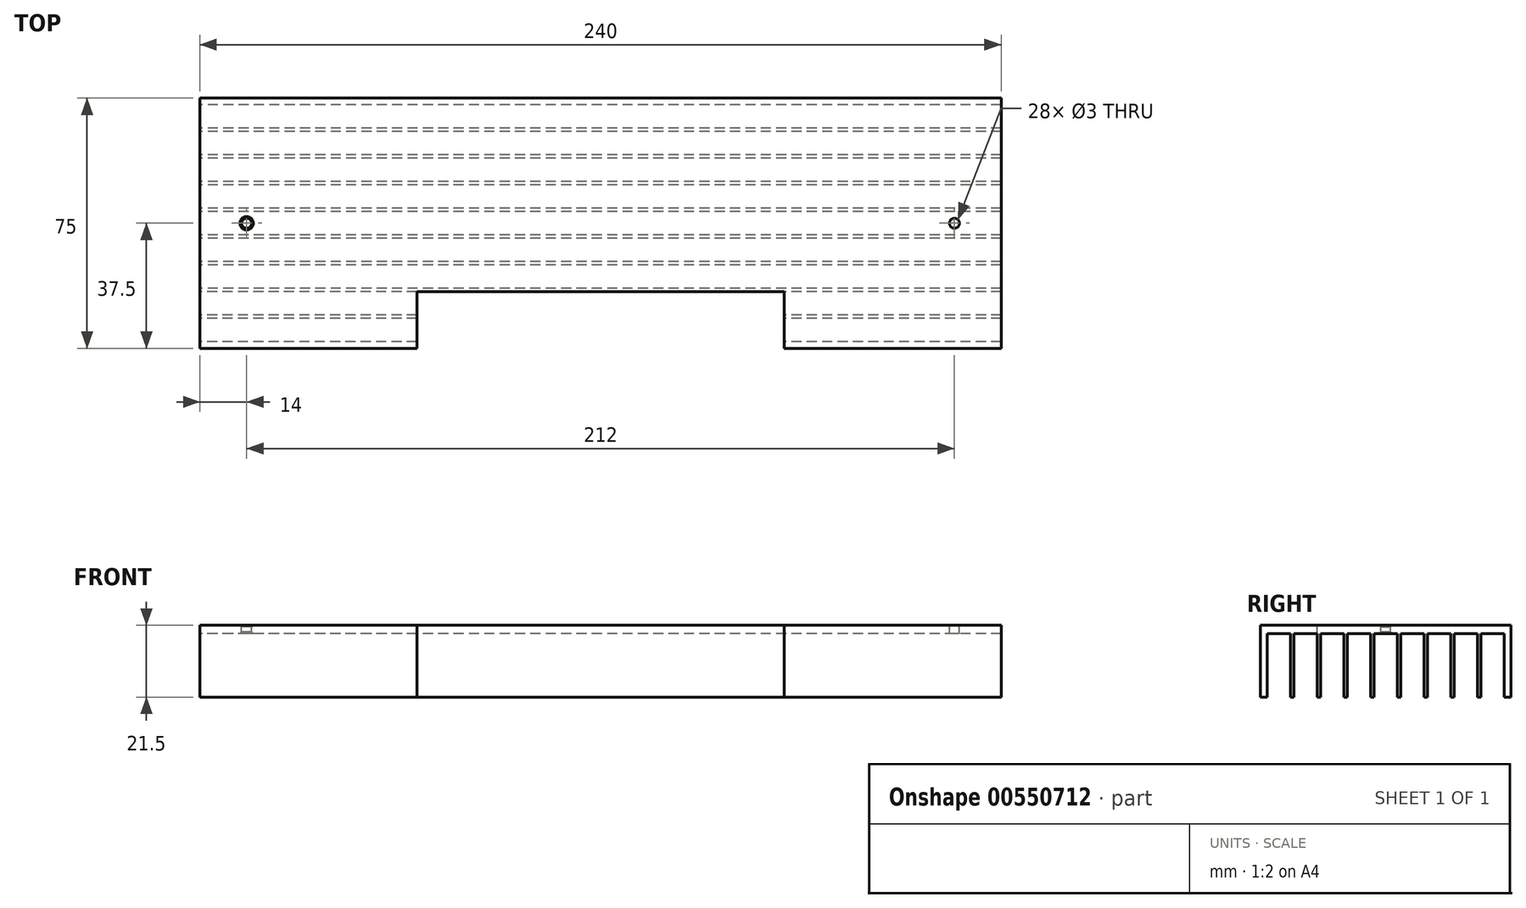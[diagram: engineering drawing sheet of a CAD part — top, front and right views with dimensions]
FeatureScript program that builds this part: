
annotation { "Feature Type Name" : "Feature", "Feature Type Description" : "" }
export const myFeature = defineFeature(function(context is Context, id is Id, definition is map)
    precondition{}
    {
        {
            var Q0;
            Q0=qCreatedBy(makeId("Right.planeOp"),FACE);
            var sketch = newSketch(context, id + "F0", { "sketchPlane" : qUnion([Q0])});
            skLineSegment(sketch, "E0.rect.bottom", {"start": v(-4.5, 9.5) * mm, "end": v(-3.5, 9.5) * mm});
            skLineSegment(sketch, "E0.rect.top", {"start": v(-4.5, -9.5) * mm, "end": v(-3.5, -9.5) * mm});
            skLineSegment(sketch, "E0.rect.left", {"start": v(-4.5, 9.5) * mm, "end": v(-4.5, -9.5) * mm});
            skLineSegment(sketch, "E0.rect.right", {"start": v(-3.5, 9.5) * mm, "end": v(-3.5, -9.5) * mm});
            skPoint(sketch, "E0.rect.middle", {"position": v(-4, 0) * mm});
            skLineSegment(sketch, "E1.rect.bottom", {"start": v(3.5, 9.5) * mm, "end": v(4.5, 9.5) * mm});
            skLineSegment(sketch, "E1.rect.top", {"start": v(3.5, -9.5) * mm, "end": v(4.5, -9.5) * mm});
            skLineSegment(sketch, "E1.rect.left", {"start": v(3.5, 9.5) * mm, "end": v(3.5, -9.5) * mm});
            skLineSegment(sketch, "E1.rect.right", {"start": v(4.5, 9.5) * mm, "end": v(4.5, -9.5) * mm});
            skPoint(sketch, "E1.rect.middle", {"position": v(4, 0) * mm});
            skLineSegment(sketch, "E2.rect.bottom", {"start": v(-12.5, 9.5) * mm, "end": v(-11.5, 9.5) * mm});
            skLineSegment(sketch, "E2.rect.top", {"start": v(-12.5, -9.5) * mm, "end": v(-11.5, -9.5) * mm});
            skLineSegment(sketch, "E2.rect.left", {"start": v(-12.5, 9.5) * mm, "end": v(-12.5, -9.5) * mm});
            skLineSegment(sketch, "E2.rect.right", {"start": v(-11.5, 9.5) * mm, "end": v(-11.5, -9.5) * mm});
            skPoint(sketch, "E2.rect.middle", {"position": v(-12, 0) * mm});
            skLineSegment(sketch, "E3.rect.bottom", {"start": v(-20.5, 9.5) * mm, "end": v(-19.5, 9.5) * mm});
            skLineSegment(sketch, "E3.rect.top", {"start": v(-20.5, -9.5) * mm, "end": v(-19.5, -9.5) * mm});
            skLineSegment(sketch, "E3.rect.left", {"start": v(-20.5, 9.5) * mm, "end": v(-20.5, -9.5) * mm});
            skLineSegment(sketch, "E3.rect.right", {"start": v(-19.5, 9.5) * mm, "end": v(-19.5, -9.5) * mm});
            skPoint(sketch, "E3.rect.middle", {"position": v(-20, 0) * mm});
            skLineSegment(sketch, "E4.rect.bottom", {"start": v(11.5, 9.5) * mm, "end": v(12.5, 9.5) * mm});
            skLineSegment(sketch, "E4.rect.top", {"start": v(11.5, -9.5) * mm, "end": v(12.5, -9.5) * mm});
            skLineSegment(sketch, "E4.rect.left", {"start": v(11.5, 9.5) * mm, "end": v(11.5, -9.5) * mm});
            skLineSegment(sketch, "E4.rect.right", {"start": v(12.5, 9.5) * mm, "end": v(12.5, -9.5) * mm});
            skPoint(sketch, "E4.rect.middle", {"position": v(12, 0) * mm});
            skLineSegment(sketch, "E5.rect.bottom", {"start": v(19.5, 9.5) * mm, "end": v(20.5, 9.5) * mm});
            skLineSegment(sketch, "E5.rect.top", {"start": v(19.5, -9.5) * mm, "end": v(20.5, -9.5) * mm});
            skLineSegment(sketch, "E5.rect.left", {"start": v(19.5, 9.5) * mm, "end": v(19.5, -9.5) * mm});
            skLineSegment(sketch, "E5.rect.right", {"start": v(20.5, 9.5) * mm, "end": v(20.5, -9.5) * mm});
            skPoint(sketch, "E5.rect.middle", {"position": v(20, 0) * mm});
            skLineSegment(sketch, "E6.rect.bottom", {"start": v(27.5, 9.5) * mm, "end": v(28.5, 9.5) * mm});
            skLineSegment(sketch, "E6.rect.top", {"start": v(27.5, -9.5) * mm, "end": v(28.5, -9.5) * mm});
            skLineSegment(sketch, "E6.rect.left", {"start": v(27.5, 9.5) * mm, "end": v(27.5, -9.5) * mm});
            skLineSegment(sketch, "E6.rect.right", {"start": v(28.5, 9.5) * mm, "end": v(28.5, -9.5) * mm});
            skPoint(sketch, "E6.rect.middle", {"position": v(28, 0) * mm});
            skLineSegment(sketch, "E7.rect.bottom", {"start": v(-28.5, 9.5) * mm, "end": v(-27.5, 9.5) * mm});
            skLineSegment(sketch, "E7.rect.top", {"start": v(-28.5, -9.5) * mm, "end": v(-27.5, -9.5) * mm});
            skLineSegment(sketch, "E7.rect.left", {"start": v(-28.5, 9.5) * mm, "end": v(-28.5, -9.5) * mm});
            skLineSegment(sketch, "E7.rect.right", {"start": v(-27.5, 9.5) * mm, "end": v(-27.5, -9.5) * mm});
            skPoint(sketch, "E7.rect.middle", {"position": v(-28, 0) * mm});
            skLineSegment(sketch, "E8", {"start": v(-27.5, -9.5) * mm, "end": v(-20.5, -9.5) * mm, "construction": true});
            skLineSegment(sketch, "E9", {"start": v(-19.5, -9.5) * mm, "end": v(-12.5, -9.5) * mm, "construction": true});
            skLineSegment(sketch, "E10", {"start": v(-11.5, -9.5) * mm, "end": v(-4.5, -9.5) * mm, "construction": true});
            skLineSegment(sketch, "E11", {"start": v(4.5, -9.5) * mm, "end": v(11.5, -9.5) * mm, "construction": true});
            skLineSegment(sketch, "E12", {"start": v(12.5, -9.5) * mm, "end": v(19.5, -9.5) * mm, "construction": true});
            skLineSegment(sketch, "E13", {"start": v(20.5, -9.5) * mm, "end": v(27.5, -9.5) * mm, "construction": true});
            skLineSegment(sketch, "E14.rect.bottom", {"start": v(37.5, 9.5) * mm, "end": v(35.5, 9.5) * mm});
            skLineSegment(sketch, "E14.rect.top", {"start": v(37.5, -9.5) * mm, "end": v(35.5, -9.5) * mm});
            skLineSegment(sketch, "E14.rect.left", {"start": v(37.5, 9.5) * mm, "end": v(37.5, -9.5) * mm});
            skLineSegment(sketch, "E14.rect.right", {"start": v(35.5, 9.5) * mm, "end": v(35.5, -9.5) * mm});
            skPoint(sketch, "E14.rect.middle", {"position": v(36.5, 0) * mm});
            skLineSegment(sketch, "E15.rect.bottom", {"start": v(-37.5, 9.5) * mm, "end": v(-35.5, 9.5) * mm});
            skLineSegment(sketch, "E15.rect.top", {"start": v(-37.5, -9.5) * mm, "end": v(-35.5, -9.5) * mm});
            skLineSegment(sketch, "E15.rect.left", {"start": v(-37.5, 9.5) * mm, "end": v(-37.5, -9.5) * mm});
            skLineSegment(sketch, "E15.rect.right", {"start": v(-35.5, 9.5) * mm, "end": v(-35.5, -9.5) * mm});
            skPoint(sketch, "E15.rect.middle", {"position": v(-36.5, 0) * mm});
            skLineSegment(sketch, "E16", {"start": v(-35.5, -9.5) * mm, "end": v(-28.5, -9.5) * mm, "construction": true});
            skLineSegment(sketch, "E17", {"start": v(28.5, -9.5) * mm, "end": v(35.5, -9.5) * mm, "construction": true});
            skLineSegment(sketch, "E18.bottom", {"start": v(-37.5, 9.5) * mm, "end": v(37.5, 9.5) * mm});
            skLineSegment(sketch, "E18.top", {"start": v(-37.5, 12) * mm, "end": v(37.5, 12) * mm});
            skLineSegment(sketch, "E18.left", {"start": v(-37.5, 9.5) * mm, "end": v(-37.5, 12) * mm});
            skLineSegment(sketch, "E18.right", {"start": v(37.5, 9.5) * mm, "end": v(37.5, 12) * mm});
            skLineSegment(sketch, "E19", {"start": v(-3.5, -9.5) * mm, "end": v(0, -9.5) * mm, "construction": true});
            skLineSegment(sketch, "E20", {"start": v(3.5, -9.5) * mm, "end": v(0, -9.5) * mm, "construction": true});
            skSolve(sketch);
        }
        {
            var Q0;
            {var subQ0=sQuery(id+"F0.wireOp",EDGE,"E15.rect.bottom");var subQ1=makeQuery(id+"F0.imprint","IMPRINT",EDGE,{"derivedFrom":subQ0});var subQ2=sQuery(id+"F0.wireOp",EDGE,"E14.rect.bottom");var subQ3=makeQuery(id+"F0.imprint","IMPRINT",EDGE,{"derivedFrom":subQ2});var subQ4=sQuery(id+"F0.wireOp",EDGE,"E7.rect.bottom");var subQ5=makeQuery(id+"F0.imprint","IMPRINT",EDGE,{"derivedFrom":subQ4});var subQ6=sQuery(id+"F0.wireOp",EDGE,"E6.rect.bottom");var subQ7=makeQuery(id+"F0.imprint","IMPRINT",EDGE,{"derivedFrom":subQ6});var subQ11=sQuery(id+"F0.wireOp",EDGE,"E5.rect.bottom");var subQ12=makeQuery(id+"F0.imprint","IMPRINT",EDGE,{"derivedFrom":subQ11});var subQ15=sQuery(id+"F0.wireOp",EDGE,"E4.rect.bottom");var subQ16=makeQuery(id+"F0.imprint","IMPRINT",EDGE,{"derivedFrom":subQ15});var subQ17=sQuery(id+"F0.wireOp",EDGE,"E0.rect.bottom");var subQ18=makeQuery(id+"F0.imprint","IMPRINT",EDGE,{"derivedFrom":subQ17});var subQ21=sQuery(id+"F0.wireOp",EDGE,"E1.rect.bottom");var subQ22=makeQuery(id+"F0.imprint","IMPRINT",EDGE,{"derivedFrom":subQ21});var subQ23=sQuery(id+"F0.wireOp",EDGE,"E2.rect.bottom");var subQ24=makeQuery(id+"F0.imprint","IMPRINT",EDGE,{"derivedFrom":subQ23});var subQ25=sQuery(id+"F0.wireOp",EDGE,"E3.rect.bottom");var subQ26=makeQuery(id+"F0.imprint","IMPRINT",EDGE,{"derivedFrom":subQ25});Q0=qUnion([makeQuery(id+"F0.imprint","IMPRINT",FACE,{"disambiguationData":[TD([[subQ18,-1.0]])]}),makeQuery(id+"F0.imprint","IMPRINT",FACE,{"disambiguationData":[TD([[subQ22,-1.0]])]}),makeQuery(id+"F0.imprint","IMPRINT",FACE,{"disambiguationData":[TD([[subQ24,-1.0]])]}),makeQuery(id+"F0.imprint","IMPRINT",FACE,{"disambiguationData":[TD([[subQ26,-1.0]])]}),makeQuery(id+"F0.imprint","IMPRINT",FACE,{"disambiguationData":[TD([[subQ16,-1.0]])]}),makeQuery(id+"F0.imprint","IMPRINT",FACE,{"disambiguationData":[TD([[subQ12,-1.0]])]}),makeQuery(id+"F0.imprint","IMPRINT",FACE,{"disambiguationData":[TD([[subQ7,-1.0]])]}),makeQuery(id+"F0.imprint","IMPRINT",FACE,{"disambiguationData":[TD([[subQ5,-1.0]])]}),makeQuery(id+"F0.imprint","IMPRINT",FACE,{"disambiguationData":[TD([[subQ3,1.0]])]}),makeQuery(id+"F0.imprint","IMPRINT",FACE,{"disambiguationData":[TD([[subQ1,-1.0]])]}),makeQuery(id+"F0.imprint","IMPRINT",FACE,{"disambiguationData":[TD([[subQ18,1.0]])]})]);}
            extrude(context, id + "F1", {"entities" : qUnion([Q0]), "depth" : 240 * mm, "symmetric" : true});
        }
        {
            var Q0;
            Q0=makeQuery(id+"F1.opExtrude","SWEPT_FACE",FACE,{"disambiguationData":[OSD([sQuery(id+"F0.wireOp",EDGE,"E18.top")])]});
            var sketch = newSketch(context, id + "F2", { "sketchPlane" : qUnion([Q0])});
            skCircle(sketch, "E21", {"center": v(-106, 0) * mm, "radius": 1.5 * mm});
            skLineSegment(sketch, "E22", {"start": v(0, 37.5) * mm, "end": v(0, -37.5) * mm, "construction": true});
            skCircle(sketch, "E23.0.MirrorC", {"center": v(106, 0) * mm, "radius": 1.5 * mm});
            skSolve(sketch);
        }
        {
            var Q0;
            Q0=qSketchRegion(id+"F2",true);
            extrude(context, id + "F3", {"entities" : qUnion([Q0]), "operationType" : NewBodyOperationType.REMOVE, "endBound" : BoundingType.THROUGH_ALL, "oppositeDirection" : true, "depth" : 42 * mm});
        }
        {
            var Q0;
            Q0=makeQuery(id+"F3.boolean.opBoolean","COPY",FACE,{"derivedFrom":makeQuery(id+"F3.opExtrude","SWEPT_FACE",FACE,{"disambiguationData":[OSD([sQuery(id+"F2.wireOp",EDGE,"E21")])]})});
            chamfer(context, id + "F4", {"entities" : qUnion([Q0]), "width" : 0.5 * mm, "tangentPropagation" : true});
        }
        {
            var Q0;
            Q0=makeQuery(id+"F1.opExtrude","SWEPT_FACE",FACE,{"disambiguationData":[OSD([sQuery(id+"F0.wireOp",EDGE,"E15.rect.left"),sQuery(id+"F0.wireOp",EDGE,"E18.left")])]});
            var sketch = newSketch(context, id + "F5", { "sketchPlane" : qUnion([Q0])});
            skLineSegment(sketch, "E24", {"start": v(0, 12) * mm, "end": v(0, -9.5) * mm, "construction": true});
            skLineSegment(sketch, "E25", {"start": v(-120, 1.25) * mm, "end": v(120, 1.25) * mm, "construction": true});
            skLineSegment(sketch, "E26.rect.bottom", {"start": v(-55, -9.5) * mm, "end": v(55, -9.5) * mm});
            skLineSegment(sketch, "E26.rect.top", {"start": v(-55, 12) * mm, "end": v(55, 12) * mm});
            skLineSegment(sketch, "E26.rect.left", {"start": v(-55, -9.5) * mm, "end": v(-55, 12) * mm});
            skLineSegment(sketch, "E26.rect.right", {"start": v(55, -9.5) * mm, "end": v(55, 12) * mm});
            skPoint(sketch, "E26.rect.middle", {"position": v(0, 1.25) * mm});
            skSolve(sketch);
        }
        {
            var Q0;
            Q0=qSketchRegion(id+"F5",true);
            extrude(context, id + "F6", {"entities" : qUnion([Q0]), "operationType" : NewBodyOperationType.REMOVE, "oppositeDirection" : true, "depth" : 17 * mm});
        }
    });
